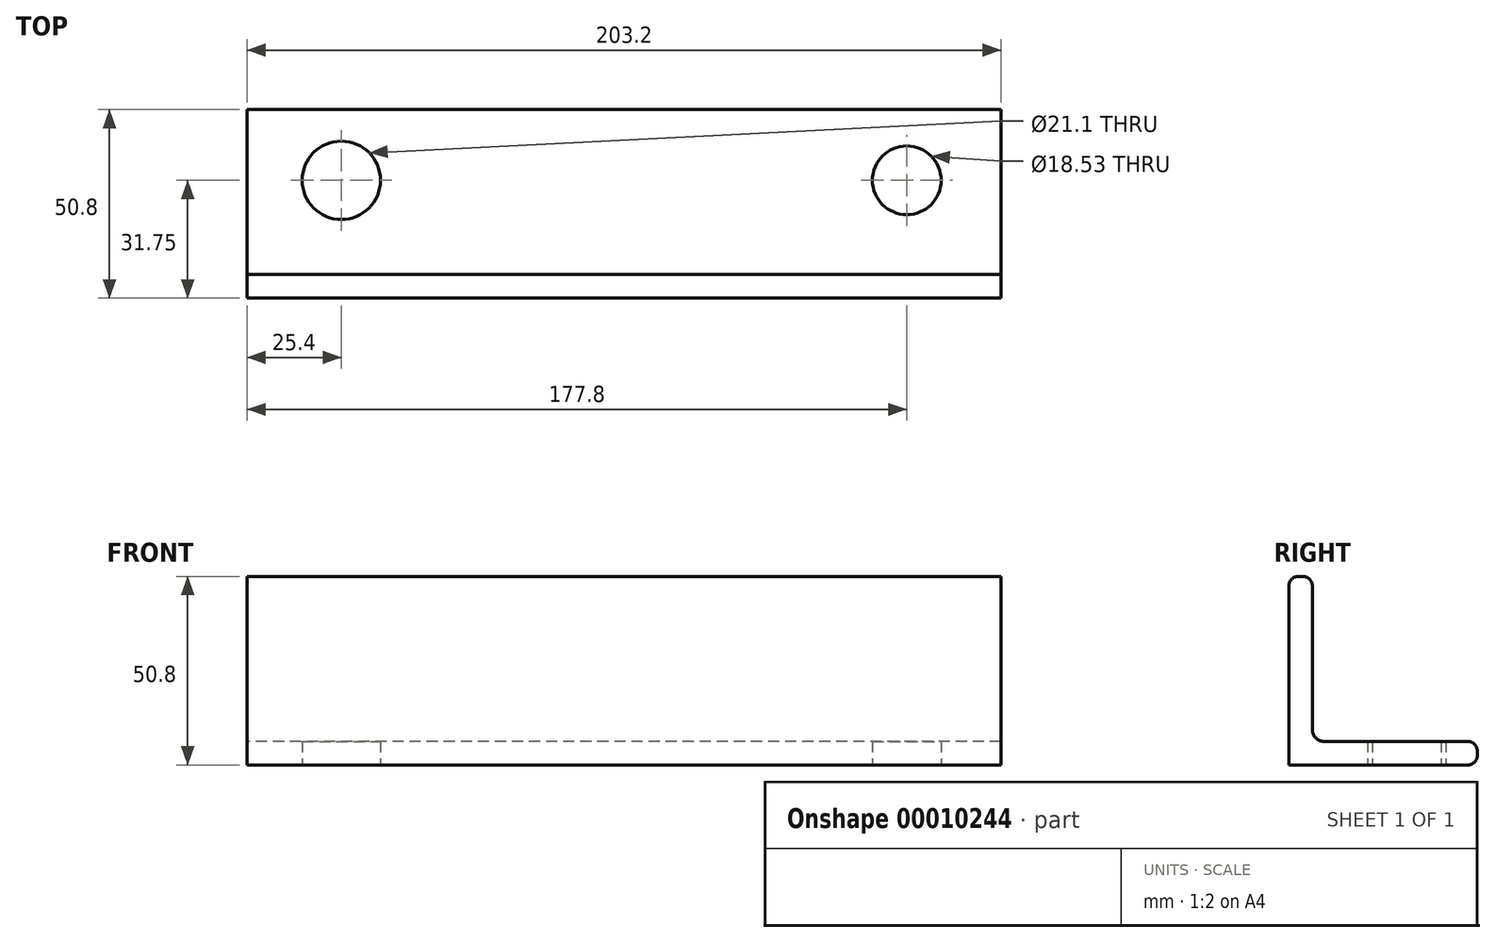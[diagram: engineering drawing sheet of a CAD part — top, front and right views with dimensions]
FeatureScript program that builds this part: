
annotation { "Feature Type Name" : "Feature", "Feature Type Description" : "" }
export const myFeature = defineFeature(function(context is Context, id is Id, definition is map)
    precondition{}
    {
        {
            var Q0;
            Q0=qCreatedBy(makeId("Right.planeOp"),FACE);
            var sketch = newSketch(context, id + "F0", { "sketchPlane" : qUnion([Q0])});
            skLineSegment(sketch, "E0", {"start": v(0, 48.26) * mm, "end": v(0, 0) * mm});
            skLineSegment(sketch, "E1", {"start": v(0, 0) * mm, "end": v(48.26, 0) * mm});
            skLineSegment(sketch, "E2", {"start": v(50.8, 2.54) * mm, "end": v(50.8, 3.81) * mm});
            skLineSegment(sketch, "E3", {"start": v(48.26, 6.35) * mm, "end": v(9.52, 6.35) * mm});
            skLineSegment(sketch, "E4", {"start": v(6.35, 9.52) * mm, "end": v(6.35, 48.26) * mm});
            skLineSegment(sketch, "E5", {"start": v(2.54, 50.8) * mm, "end": v(3.8, 50.8) * mm});
            skPoint(sketch, "E6.visualSharp", {"position": v(6.35, 6.35) * mm});
            skArc(sketch, "E6.filletArc", {"start": v(6.35, 9.52) * mm, "mid": v(7.28, 7.28) * mm, "end": v(9.52, 6.35) * mm});
            skPoint(sketch, "E7.visualSharp", {"position": v(50.8, 6.35) * mm});
            skArc(sketch, "E7.filletArc", {"start": v(50.8, 3.81) * mm, "mid": v(50.06, 5.6) * mm, "end": v(48.26, 6.35) * mm});
            skPoint(sketch, "E8.visualSharp", {"position": v(6.35, 50.8) * mm});
            skArc(sketch, "E8.filletArc", {"start": v(6.35, 48.26) * mm, "mid": v(5.6, 50.06) * mm, "end": v(3.8, 50.8) * mm});
            skPoint(sketch, "E9.visualSharp", {"position": v(0, 50.8) * mm});
            skArc(sketch, "E9.filletArc", {"start": v(2.54, 50.8) * mm, "mid": v(0.74, 50.06) * mm, "end": v(0, 48.26) * mm});
            skPoint(sketch, "E10.visualSharp", {"position": v(50.8, 0) * mm});
            skArc(sketch, "E10.filletArc", {"start": v(48.26, 0) * mm, "mid": v(50.06, 0.74) * mm, "end": v(50.8, 2.54) * mm});
            skSolve(sketch);
        }
        {
            var Q0;
            Q0=makeQuery(id+"F0.imprint","IMPRINT",FACE,{"disambiguationData":[TD([[makeQuery(id+"F0.imprint","IMPRINT",EDGE,{"derivedFrom":sQuery(id+"F0.wireOp",EDGE,"E0")}),1.0]])]});
            extrude(context, id + "F1", {"entities" : qUnion([Q0]), "depth" : 203.2 * mm});
        }
        {
            var Q0;
            Q0=makeQuery(id+"F1.opExtrude","SWEPT_FACE",FACE,{"disambiguationData":[OSD([sQuery(id+"F0.wireOp",EDGE,"E1")])]});
            var sketch = newSketch(context, id + "F2", { "sketchPlane" : qUnion([Q0])});
            skCircle(sketch, "E11", {"center": v(177.8, -31.75) * mm, "radius": 9.26 * mm});
            skCircle(sketch, "E12", {"center": v(25.4, -31.75) * mm, "radius": 10.55 * mm});
            skSolve(sketch);
        }
        {
            var Q0;
            Q0 = qSketchRegion(id + "F2", true);
            extrude(context, id + "F3", {"entities" : qUnion([Q0]), "operationType" : NewBodyOperationType.REMOVE, "oppositeDirection" : true, "depth" : 25.4 * mm});
        }
    });
